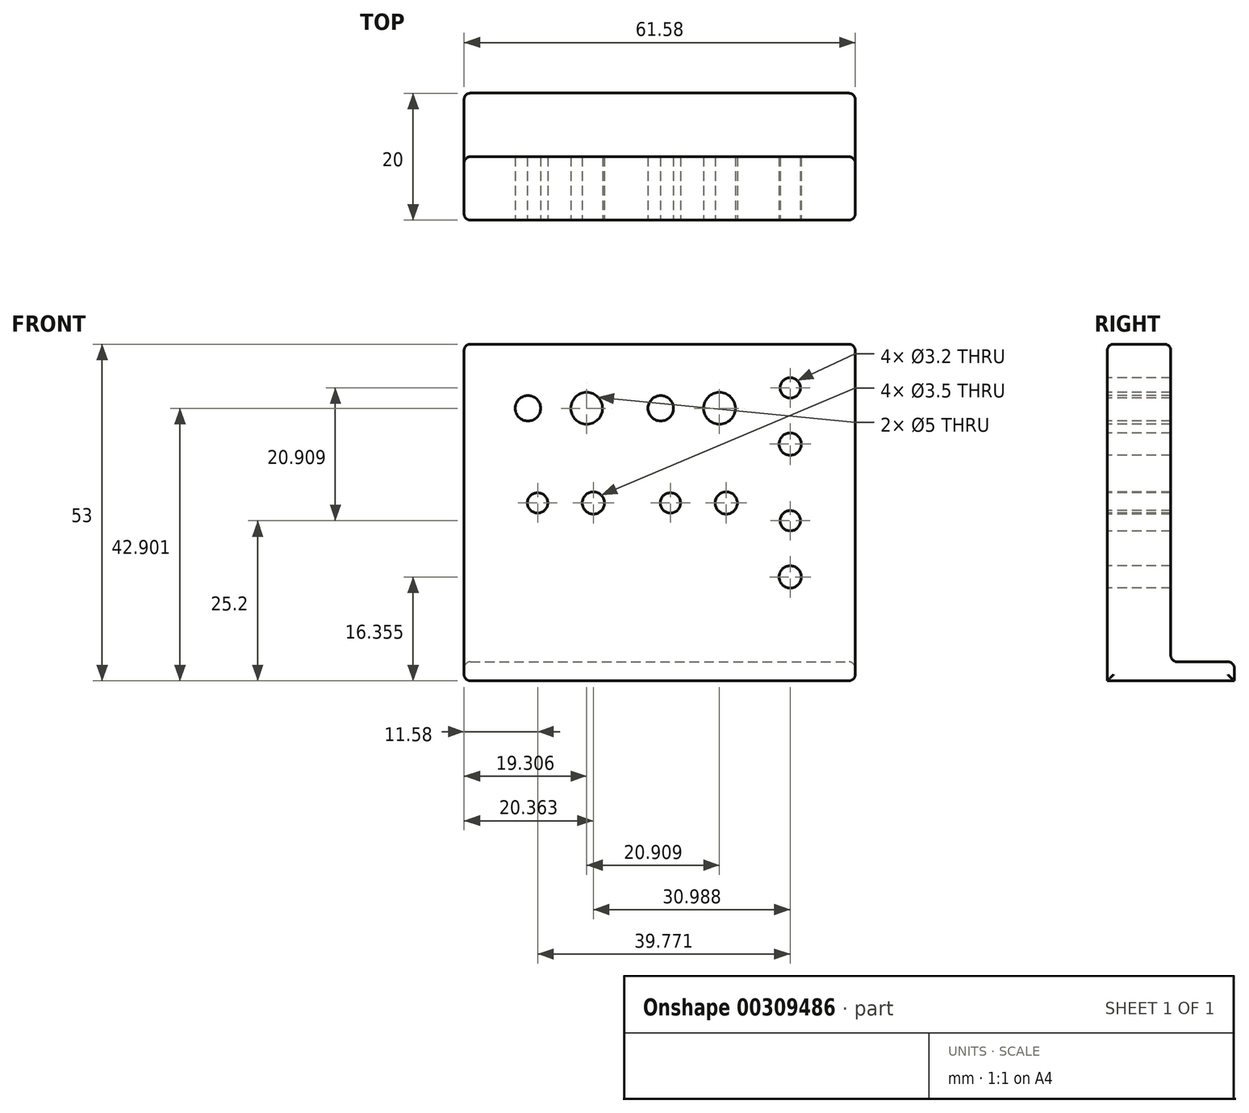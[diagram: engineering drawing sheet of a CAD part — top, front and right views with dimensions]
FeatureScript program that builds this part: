
annotation { "Feature Type Name" : "Feature", "Feature Type Description" : "" }
export const myFeature = defineFeature(function(context is Context, id is Id, definition is map)
    precondition{}
    {
        {
            var Q0;
            Q0=qCreatedBy(makeId("Top.planeOp"),FACE);
            var sketch = newSketch(context, id + "F0", { "sketchPlane" : qUnion([Q0])});
            skLineSegment(sketch, "E0.bottom", {"start": v(50, 25) * mm, "end": v(-50, 25) * mm});
            skLineSegment(sketch, "E0.top", {"start": v(50, -25) * mm, "end": v(-50, -25) * mm});
            skLineSegment(sketch, "E0.left", {"start": v(50, 25) * mm, "end": v(50, -25) * mm});
            skLineSegment(sketch, "E0.right", {"start": v(-50, 25) * mm, "end": v(-50, -25) * mm});
            skPoint(sketch, "E0.middle", {"position": v(0, 0) * mm});
            skLineSegment(sketch, "E1", {"start": v(-50, 20.14) * mm, "end": v(50, 20.14) * mm});
            skLineSegment(sketch, "E2.0.1.0", {"start": v(-50, 15.14) * mm, "end": v(50, 15.14) * mm});
            skLineSegment(sketch, "E2.0.2.0", {"start": v(-50, 10.14) * mm, "end": v(50, 10.14) * mm});
            skLineSegment(sketch, "E2.0.3.0", {"start": v(-50, 5.14) * mm, "end": v(50, 5.14) * mm});
            skLineSegment(sketch, "E2.0.4.0", {"start": v(-50, 0.14) * mm, "end": v(50, 0.14) * mm});
            skLineSegment(sketch, "E2.0.5.0", {"start": v(-50, -4.86) * mm, "end": v(50, -4.86) * mm});
            skLineSegment(sketch, "E2.0.6.0", {"start": v(-50, -9.86) * mm, "end": v(50, -9.86) * mm});
            skLineSegment(sketch, "E2.0.7.0", {"start": v(-50, -14.86) * mm, "end": v(50, -14.86) * mm});
            skLineSegment(sketch, "E2.0.8.0", {"start": v(-50, -19.86) * mm, "end": v(50, -19.86) * mm});
            skLineSegment(sketch, "E2.direction1", {"start": v(-50, 20.14) * mm, "end": v(-24.9, 20.14) * mm, "construction": true});
            skLineSegment(sketch, "E2.direction2", {"start": v(-50, 20.14) * mm, "end": v(-50, 15.14) * mm, "construction": true});
            skSolve(sketch);
        }
        {
            var Q0;
            {var subQ0=sQuery(id+"F0.wireOp",EDGE,"E2.0.1.0");Q0=makeQuery(id+"F0.imprint","IMPRINT",FACE,{"disambiguationData":[TD([[makeQuery(id+"F0.imprint","IMPRINT",EDGE,{"derivedFrom":subQ0}),-1.0]])]});}
            var Q1;
            {var subQ0=sQuery(id+"F0.wireOp",EDGE,"E2.0.2.0");Q1=makeQuery(id+"F0.imprint","IMPRINT",FACE,{"disambiguationData":[TD([[makeQuery(id+"F0.imprint","IMPRINT",EDGE,{"derivedFrom":subQ0}),-1.0]])]});}
            var Q2;
            {var subQ0=sQuery(id+"F0.wireOp",EDGE,"E2.0.3.0");Q2=makeQuery(id+"F0.imprint","IMPRINT",FACE,{"disambiguationData":[TD([[makeQuery(id+"F0.imprint","IMPRINT",EDGE,{"derivedFrom":subQ0}),-1.0]])]});}
            var Q3;
            {var subQ0=sQuery(id+"F0.wireOp",EDGE,"E2.0.4.0");Q3=makeQuery(id+"F0.imprint","IMPRINT",FACE,{"disambiguationData":[TD([[makeQuery(id+"F0.imprint","IMPRINT",EDGE,{"derivedFrom":subQ0}),-1.0]])]});}
            extrude(context, id + "F1", {"entities" : qUnion([Q0, Q1, Q2, Q3]), "depth" : 3 * mm});
        }
        {
            var Q0;
            Q0=makeQuery(id+"F1.opExtrude","CAP_FACE",FACE,{"disambiguationData":[OSD([sQuery(id+"F0.wireOp",EDGE,"E0.bottom"),sQuery(id+"F0.wireOp",EDGE,"E0.top"),sQuery(id+"F0.wireOp",EDGE,"E0.left"),sQuery(id+"F0.wireOp",EDGE,"E0.right")])],"isStart":false});
            var sketch = newSketch(context, id + "F2", { "sketchPlane" : qUnion([Q0])});
            skLineSegment(sketch, "E3.0", {"start": v(-50, -4.86) * mm, "end": v(50, -4.86) * mm});
            skLineSegment(sketch, "E3.1", {"start": v(-50, 5.14) * mm, "end": v(50, 5.14) * mm});
            skLineSegment(sketch, "E3.2", {"start": v(-50, 15.14) * mm, "end": v(-50, 15.14) * mm});
            skLineSegment(sketch, "E3.3", {"start": v(50, 25) * mm, "end": v(50, -25) * mm});
            skLineSegment(sketch, "E4.0", {"start": v(-50, -19.86) * mm, "end": v(50, -19.86) * mm});
            skLineSegment(sketch, "E4.1", {"start": v(-50, -14.86) * mm, "end": v(50, -14.86) * mm});
            skLineSegment(sketch, "E4.2", {"start": v(-50, 15.14) * mm, "end": v(50, 15.14) * mm});
            skLineSegment(sketch, "E4.3", {"start": v(-50, 20.14) * mm, "end": v(50, 20.14) * mm});
            skSolve(sketch);
        }
        {
            var Q0;
            {var subQ0=sQuery(id+"F2.wireOp",EDGE,"E3.0");Q0=makeQuery(id+"F2.imprint","IMPRINT",FACE,{"disambiguationData":[TD([[makeQuery(id+"F2.imprint","IMPRINT",EDGE,{"derivedFrom":subQ0}),1.0]])]});}
            var Q1;
            {var subQ0=sQuery(id+"F2.wireOp",EDGE,"E4.0");Q1=makeQuery(id+"F2.imprint","IMPRINT",FACE,{"disambiguationData":[TD([[makeQuery(id+"F2.imprint","IMPRINT",EDGE,{"derivedFrom":subQ0}),1.0]])]});}
            var Q2;
            {var subQ0=sQuery(id+"F2.wireOp",EDGE,"E4.2");Q2=makeQuery(id+"F2.imprint","IMPRINT",FACE,{"disambiguationData":[TD([[makeQuery(id+"F2.imprint","IMPRINT",EDGE,{"derivedFrom":subQ0}),1.0]])]});}
            extrude(context, id + "F3", {"entities" : qUnion([Q0, Q1, Q2]), "operationType" : NewBodyOperationType.ADD, "depth" : 50 * mm});
        }
        {
            var Q0;
            Q0=makeQuery(id+"F3.opExtrude","SWEPT_FACE",FACE,{"disambiguationData":[OSD([sQuery(id+"F2.wireOp",EDGE,"E3.0")])]});
            var sketch = newSketch(context, id + "F4", { "sketchPlane" : qUnion([Q0])});
            skLineSegment(sketch, "E5.1", {"start": v(-50, 53) * mm, "end": v(-50, 3) * mm});
            skLineSegment(sketch, "E5.2", {"start": v(-50, 53) * mm, "end": v(50, 53) * mm});
            skLineSegment(sketch, "E5.3", {"start": v(50, 3) * mm, "end": v(50, 53) * mm});
            skLineSegment(sketch, "E6", {"start": v(-50, 3) * mm, "end": v(50, 3) * mm});
            skCircle(sketch, "E7", {"center": v(0, 28) * mm, "radius": 1.6 * mm});
            skPoint(sketch, "E7.centerSnap0", {"position": v(-50, 28) * mm});
            skCircle(sketch, "E8", {"center": v(20.9, 28) * mm, "radius": 1.6 * mm});
            skCircle(sketch, "E9", {"center": v(8.78, 28) * mm, "radius": 1.75 * mm});
            skCircle(sketch, "E10", {"center": v(29.7, 28) * mm, "radius": 1.75 * mm});
            skCircle(sketch, "E11", {"center": v(39.77, 46.1) * mm, "radius": 1.6 * mm});
            skCircle(sketch, "E12", {"center": v(39.77, 25.2) * mm, "radius": 1.6 * mm});
            skCircle(sketch, "E13", {"center": v(39.77, 37.26) * mm, "radius": 1.75 * mm});
            skCircle(sketch, "E14", {"center": v(39.77, 16.36) * mm, "radius": 1.75 * mm});
            skCircle(sketch, "E15", {"center": v(7.73, 42.9) * mm, "radius": 2.5 * mm});
            skCircle(sketch, "E16", {"center": v(28.63, 42.9) * mm, "radius": 2.5 * mm});
            skCircle(sketch, "E17", {"center": v(-1.52, 42.9) * mm, "radius": 2 * mm});
            skCircle(sketch, "E18", {"center": v(19.39, 42.9) * mm, "radius": 2 * mm});
            skSolve(sketch);
        }
        {
            var Q0;
            Q0=makeQuery(id+"F4.imprint","IMPRINT",FACE,{"disambiguationData":[TD([[makeQuery(id+"F4.imprint","IMPRINT",EDGE,{"derivedFrom":sQuery(id+"F4.wireOp",EDGE,"E7")}),1.0]])]});
            var Q1;
            Q1=makeQuery(id+"F4.imprint","IMPRINT",FACE,{"disambiguationData":[TD([[makeQuery(id+"F4.imprint","IMPRINT",EDGE,{"derivedFrom":sQuery(id+"F4.wireOp",EDGE,"E12")}),1.0]])]});
            var Q2;
            Q2=makeQuery(id+"F4.imprint","IMPRINT",FACE,{"disambiguationData":[TD([[makeQuery(id+"F4.imprint","IMPRINT",EDGE,{"derivedFrom":sQuery(id+"F4.wireOp",EDGE,"E9")}),1.0]])]});
            var Q3;
            Q3=makeQuery(id+"F4.imprint","IMPRINT",FACE,{"disambiguationData":[TD([[makeQuery(id+"F4.imprint","IMPRINT",EDGE,{"derivedFrom":sQuery(id+"F4.wireOp",EDGE,"E13")}),1.0]])]});
            var Q4;
            Q4=makeQuery(id+"F4.imprint","IMPRINT",FACE,{"disambiguationData":[TD([[makeQuery(id+"F4.imprint","IMPRINT",EDGE,{"derivedFrom":sQuery(id+"F4.wireOp",EDGE,"E8")}),1.0]])]});
            var Q5;
            Q5=makeQuery(id+"F4.imprint","IMPRINT",FACE,{"disambiguationData":[TD([[makeQuery(id+"F4.imprint","IMPRINT",EDGE,{"derivedFrom":sQuery(id+"F4.wireOp",EDGE,"E10")}),1.0]])]});
            var Q6;
            Q6=makeQuery(id+"F4.imprint","IMPRINT",FACE,{"disambiguationData":[TD([[makeQuery(id+"F4.imprint","IMPRINT",EDGE,{"derivedFrom":sQuery(id+"F4.wireOp",EDGE,"E11")}),1.0]])]});
            var Q7;
            Q7=makeQuery(id+"F4.imprint","IMPRINT",FACE,{"disambiguationData":[TD([[makeQuery(id+"F4.imprint","IMPRINT",EDGE,{"derivedFrom":sQuery(id+"F4.wireOp",EDGE,"E14")}),1.0]])]});
            var Q8;
            Q8=makeQuery(id+"F4.imprint","IMPRINT",FACE,{"disambiguationData":[TD([[makeQuery(id+"F4.imprint","IMPRINT",EDGE,{"derivedFrom":sQuery(id+"F4.wireOp",EDGE,"E15")}),1.0]])]});
            var Q9;
            Q9=makeQuery(id+"F4.imprint","IMPRINT",FACE,{"disambiguationData":[TD([[makeQuery(id+"F4.imprint","IMPRINT",EDGE,{"derivedFrom":sQuery(id+"F4.wireOp",EDGE,"E16")}),1.0]])]});
            var Q10;
            Q10=makeQuery(id+"F4.imprint","IMPRINT",FACE,{"disambiguationData":[TD([[makeQuery(id+"F4.imprint","IMPRINT",EDGE,{"derivedFrom":sQuery(id+"F4.wireOp",EDGE,"E17")}),1.0]])]});
            var Q11;
            Q11=makeQuery(id+"F4.imprint","IMPRINT",FACE,{"disambiguationData":[TD([[makeQuery(id+"F4.imprint","IMPRINT",EDGE,{"derivedFrom":sQuery(id+"F4.wireOp",EDGE,"E18")}),1.0]])]});
            extrude(context, id + "F5", {"entities" : qUnion([Q0, Q1, Q2, Q3, Q4, Q5, Q6, Q7, Q8, Q9, Q10, Q11]), "operationType" : NewBodyOperationType.REMOVE, "oppositeDirection" : true, "depth" : 50 * mm});
        }
        {
            var Q0;
            Q0=makeQuery(id+"F3.opExtrude","SWEPT_FACE",FACE,{"disambiguationData":[OSD([sQuery(id+"F2.wireOp",EDGE,"E3.0")])]});
            var sketch = newSketch(context, id + "F6", { "sketchPlane" : qUnion([Q0])});
            skLineSegment(sketch, "E19", {"start": v(-11.58, 49.9) * mm, "end": v(-11.58, 62.56) * mm});
            skLineSegment(sketch, "E20", {"start": v(-11.58, 62.56) * mm, "end": v(-11.58, -17.87) * mm});
            skLineSegment(sketch, "E21", {"start": v(-11.58, 62.56) * mm, "end": v(-61.6, 62.56) * mm});
            skLineSegment(sketch, "E22", {"start": v(-61.6, 62.56) * mm, "end": v(-61.6, -15.4) * mm});
            skLineSegment(sketch, "E23", {"start": v(-61.6, -15.4) * mm, "end": v(-11.58, -17.87) * mm});
            skSolve(sketch);
        }
        {
            var Q0;
            {var subQ0=sQuery(id+"F6.wireOp",EDGE,"E21");Q0=makeQuery(id+"F6.imprint","IMPRINT",FACE,{"disambiguationData":[TD([[makeQuery(id+"F6.imprint","IMPRINT",EDGE,{"derivedFrom":subQ0}),1.0]])]});}
            var Q1;
            {var subQ0=sQuery(id+"F2.wireOp",EDGE,"E3.0");var subQ2=makeQuery(id+"F3.opExtrude","SWEPT_EDGE",EDGE,{"disambiguationData":[OSD([sQuery(id+"F0.wireOp",EDGE,"E0.right"),subQ0])]});Q1=makeQuery(id+"F6.imprint","IMPRINT",FACE,{"disambiguationData":[TD([[makeQuery(id+"F6.imprint","IMPRINT",EDGE,{"derivedFrom":subQ2}),1.0]])]});}
            extrude(context, id + "F7", {"entities" : qUnion([Q0, Q1]), "operationType" : NewBodyOperationType.REMOVE, "oppositeDirection" : true, "depth" : 50 * mm, "hasSecondDirection" : true, "secondDirectionOppositeDirection" : false, "secondDirectionDepth" : 25 * mm});
        }
        {
            var Q0;
            {var subQ0=sQuery(id+"F2.wireOp",EDGE,"E3.3");var subQ1=sQuery(id+"F0.wireOp",EDGE,"E0.left");var subQ2=makeQuery(id+"F0.imprint","INTERSECT",VERTEX,{"derivedFrom":[subQ1,sQuery(id+"F0.wireOp",EDGE,"E2.0.4.0")]});Q0=makeQuery(id+"F3.boolean.opBoolean","MERGE",FACE,{"derivedFrom":[makeQuery(id+"F7sIhfZgX3qDGKo_0.boolean.opBoolean","MERGE",FACE,{"derivedFrom":[makeQuery(id+"F1.opExtrude","SWEPT_FACE",FACE,{"disambiguationData":[OSD([subQ1])]}),makeQuery(id+"F7sIhfZgX3qDGKo_0.opExtrude","SWEPT_FACE",FACE,{"disambiguationData":[OSD([subQ1]),TDD([makeQuery(id+"F0.imprint","IMPRINT",EDGE,{"disambiguationData":[TD([[makeQuery(id+"F0.imprint","INTERSECT",VERTEX,{"derivedFrom":[sQuery(id+"F0.wireOp",EDGE,"E0.bottom"),subQ1]}),-1.0]])],"derivedFrom":subQ1})])]}),makeQuery(id+"F7sIhfZgX3qDGKo_0.opExtrude","SWEPT_FACE",FACE,{"disambiguationData":[OSD([subQ1]),TDD([makeQuery(id+"F0.imprint","IMPRINT",EDGE,{"disambiguationData":[TD([[makeQuery(id+"F0.imprint","INTERSECT",VERTEX,{"derivedFrom":[subQ1,sQuery(id+"F0.wireOp",EDGE,"E2.0.1.0")]}),-1.0]])],"derivedFrom":subQ1})])]}),makeQuery(id+"F7sIhfZgX3qDGKo_0.opExtrude","SWEPT_FACE",FACE,{"disambiguationData":[OSD([subQ1]),TDD([makeQuery(id+"F0.imprint","IMPRINT",EDGE,{"disambiguationData":[TD([[makeQuery(id+"F0.imprint","INTERSECT",VERTEX,{"derivedFrom":[subQ1,sQuery(id+"F0.wireOp",EDGE,"E2.0.3.0")]}),-1.0]])],"derivedFrom":subQ1}),makeQuery(id+"F0.imprint","IMPRINT",EDGE,{"disambiguationData":[TD([[subQ2,-1.0]])],"derivedFrom":subQ1})])]}),makeQuery(id+"F7sIhfZgX3qDGKo_0.opExtrude","SWEPT_FACE",FACE,{"disambiguationData":[OSD([subQ1]),TDD([makeQuery(id+"F0.imprint","IMPRINT",EDGE,{"disambiguationData":[TD([[makeQuery(id+"F0.imprint","INTERSECT",VERTEX,{"derivedFrom":[subQ1,sQuery(id+"F0.wireOp",EDGE,"E2.0.6.0")]}),-1.0]])],"derivedFrom":subQ1})])]}),makeQuery(id+"F7sIhfZgX3qDGKo_0.opExtrude","SWEPT_FACE",FACE,{"disambiguationData":[OSD([subQ1]),TDD([makeQuery(id+"F0.imprint","IMPRINT",EDGE,{"disambiguationData":[TD([[makeQuery(id+"F0.imprint","INTERSECT",VERTEX,{"derivedFrom":[sQuery(id+"F0.wireOp",EDGE,"E0.top"),subQ1]}),1.0]])],"derivedFrom":subQ1})])]})]}),makeQuery(id+"F3.opExtrude","SWEPT_FACE",FACE,{"disambiguationData":[OSD([subQ0]),TDD([makeQuery(id+"F2.imprint","IMPRINT",EDGE,{"disambiguationData":[TD([[makeQuery(id+"F2.imprint","INTERSECT",VERTEX,{"derivedFrom":[subQ0,sQuery(id+"F2.wireOp",EDGE,"E4.2")]}),1.0]])],"derivedFrom":subQ0})])]}),makeQuery(id+"F3.opExtrude","SWEPT_FACE",FACE,{"disambiguationData":[OSD([subQ0]),TDD([makeQuery(id+"F2.imprint","IMPRINT",EDGE,{"disambiguationData":[TD([[makeQuery(id+"F2.imprint","INTERSECT",VERTEX,{"derivedFrom":[sQuery(id+"F2.wireOp",EDGE,"E3.0"),subQ0]}),1.0]])],"derivedFrom":subQ0})])]}),makeQuery(id+"F3.opExtrude","SWEPT_FACE",FACE,{"disambiguationData":[OSD([subQ0]),TDD([makeQuery(id+"F2.imprint","IMPRINT",EDGE,{"disambiguationData":[TD([[makeQuery(id+"F2.imprint","INTERSECT",VERTEX,{"derivedFrom":[subQ0,sQuery(id+"F2.wireOp",EDGE,"E4.0")]}),1.0]])],"derivedFrom":subQ0})])]})]});}
            var Q1;
            Q1=makeQuery(id+"F3.opExtrude","CAP_FACE",FACE,{"disambiguationData":[OSD([sQuery(id+"F2.wireOp",EDGE,"E3.0"),sQuery(id+"F2.wireOp",EDGE,"E3.1"),sQuery(id+"F2.wireOp",EDGE,"E3.2"),sQuery(id+"F2.wireOp",EDGE,"E3.3")])],"isStart":false});
            var Q2;
            Q2=makeQuery(id+"F3.opExtrude","CAP_FACE",FACE,{"disambiguationData":[OSD([sQuery(id+"F2.wireOp",EDGE,"E3.2"),sQuery(id+"F2.wireOp",EDGE,"E3.3"),sQuery(id+"F2.wireOp",EDGE,"E4.0"),sQuery(id+"F2.wireOp",EDGE,"E4.1")])],"isStart":false});
            var Q3;
            Q3=makeQuery(id+"F3.opExtrude","CAP_FACE",FACE,{"disambiguationData":[OSD([sQuery(id+"F2.wireOp",EDGE,"E3.2"),sQuery(id+"F2.wireOp",EDGE,"E3.3"),sQuery(id+"F2.wireOp",EDGE,"E4.2"),sQuery(id+"F2.wireOp",EDGE,"E4.3")])],"isStart":false});
            var Q4;
            Q4=makeQuery(id+"F7.boolean.opBoolean","COPY",FACE,{"derivedFrom":makeQuery(id+"F7.opExtrude","SWEPT_FACE",FACE,{"disambiguationData":[OSD([sQuery(id+"F6.wireOp",EDGE,"E20")])]})});
            var Q5;
            {var subQ0=sQuery(id+"F0.wireOp",EDGE,"E0.left");var subQ1=sQuery(id+"F0.wireOp",EDGE,"E0.top");var subQ9=sQuery(id+"F0.wireOp",EDGE,"E0.right");var subQ10=sQuery(id+"F0.wireOp",EDGE,"E0.bottom");Q5=makeQuery(id+"F3.boolean.opBoolean","SPLIT",FACE,{"disambiguationData":[TD([makeQuery(id+"F1.opExtrude","SWEPT_FACE",FACE,{"disambiguationData":[OSD([subQ10])]})])],"derivedFrom":makeQuery(id+"F1.opExtrude","CAP_FACE",FACE,{"disambiguationData":[OSD([subQ10,subQ1,subQ0,subQ9])],"isStart":false})});}
            var Q6;
            Q6=makeQuery(id+"F3.opExtrude","CAP_EDGE",EDGE,{"disambiguationData":[OSD([sQuery(id+"F2.wireOp",EDGE,"E4.0")])],"isStart":true});
            var Q7;
            {var subQ0=sQuery(id+"F0.wireOp",EDGE,"E0.left");var subQ1=sQuery(id+"F0.wireOp",EDGE,"E0.top");var subQ7=sQuery(id+"F0.wireOp",EDGE,"E0.right");var subQ8=sQuery(id+"F0.wireOp",EDGE,"E0.bottom");Q7=makeQuery(id+"F3.boolean.opBoolean","SPLIT",FACE,{"disambiguationData":[TD([makeQuery(id+"F1.opExtrude","SWEPT_FACE",FACE,{"disambiguationData":[OSD([subQ1])]})])],"derivedFrom":makeQuery(id+"F1.opExtrude","CAP_FACE",FACE,{"disambiguationData":[OSD([subQ8,subQ1,subQ0,subQ7])],"isStart":false})});}
            var Q8;
            Q8=makeQuery(id+"F3.opExtrude","SWEPT_FACE",FACE,{"disambiguationData":[OSD([sQuery(id+"F2.wireOp",EDGE,"E4.0")])]});
            var Q9;
            Q9=makeQuery(id+"F3.opExtrude","SWEPT_FACE",FACE,{"disambiguationData":[OSD([sQuery(id+"F2.wireOp",EDGE,"E4.3")])]});
            fillet(context, id + "F8", {"entities" : qUnion([Q0, Q1, Q2, Q3, Q4, Q5, Q6, Q7, Q8, Q9]), "radius" : 1 * mm, "tangentPropagation" : true, "allowEdgeOverflow" : false});
        }
    });
